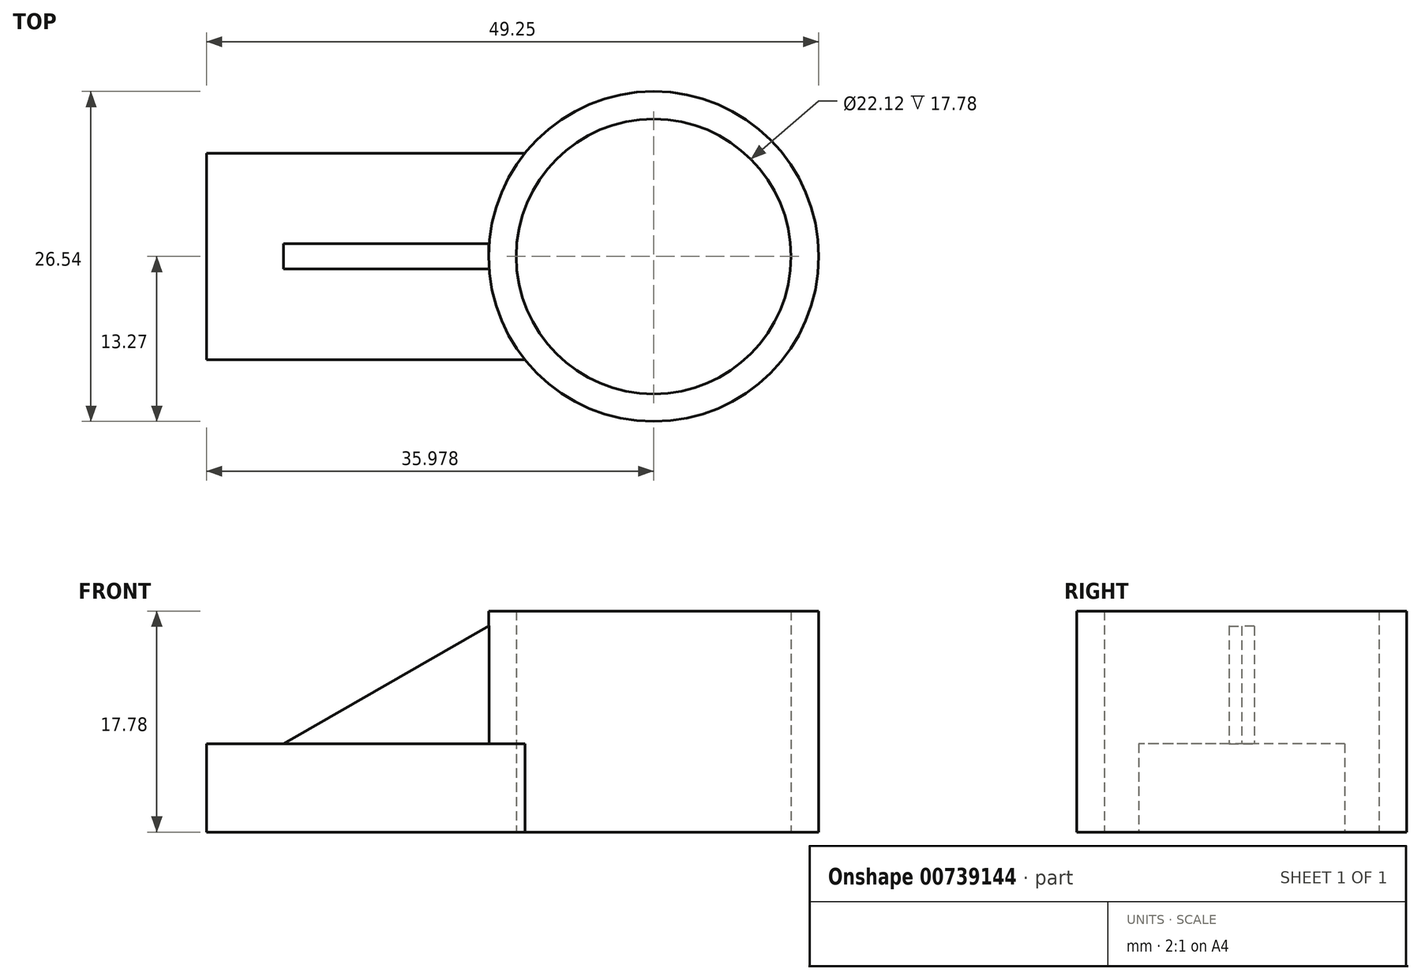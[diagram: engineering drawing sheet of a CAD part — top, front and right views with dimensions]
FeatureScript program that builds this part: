
annotation { "Feature Type Name" : "Feature", "Feature Type Description" : "" }
export const myFeature = defineFeature(function(context is Context, id is Id, definition is map)
    precondition{}
    {
        {
            var Q0;
            Q0=qCreatedBy(makeId("Top.planeOp"),FACE);
            var sketch = newSketch(context, id + "F0", { "sketchPlane" : qUnion([Q0])});
            skLineSegment(sketch, "E0.bottom", {"start": v(16.99, 8.3) * mm, "end": v(-18.99, 8.3) * mm});
            skLineSegment(sketch, "E0.top", {"start": v(16.99, -8.3) * mm, "end": v(-18.99, -8.3) * mm});
            skLineSegment(sketch, "E0.left", {"start": v(16.99, 8.3) * mm, "end": v(16.99, -8.3) * mm});
            skLineSegment(sketch, "E0.right", {"start": v(-18.99, 8.3) * mm, "end": v(-18.99, -8.3) * mm});
            skPoint(sketch, "E0.middle", {"position": v(0, 0) * mm});
            skCircle(sketch, "E1", {"center": v(16.99, 0) * mm, "radius": 13.27 * mm});
            skCircle(sketch, "E2", {"center": v(16.99, 0) * mm, "radius": 11.06 * mm});
            skSolve(sketch);
        }
        {
            var Q0;
            {var subQ0=sQuery(id+"F0.wireOp",EDGE,"E0.right");Q0=makeQuery(id+"F0.imprint","IMPRINT",FACE,{"disambiguationData":[TD([[makeQuery(id+"F0.imprint","IMPRINT",EDGE,{"derivedFrom":subQ0}),1.0]])]});}
            extrude(context, id + "F1", {"entities" : qUnion([Q0]), "depth" : 7.11 * mm, "offsetDistance" : 25.4 * mm});
        }
        {
            var Q0;
            {var subQ0=sQuery(id+"F0.wireOp",EDGE,"E1");var subQ1=sQuery(id+"F0.wireOp",EDGE,"E0.bottom");var subQ2=makeQuery(id+"F0.imprint","INTERSECT",VERTEX,{"derivedFrom":[subQ1,subQ0]});Q0=makeQuery(id+"F0.imprint","IMPRINT",FACE,{"disambiguationData":[TD([[makeQuery(id+"F0.imprint","IMPRINT",EDGE,{"disambiguationData":[TD([[subQ2,1.0]])],"derivedFrom":subQ1}),-1.0]])]});}
            var Q1;
            {var subQ0=sQuery(id+"F0.wireOp",EDGE,"E1");var subQ1=sQuery(id+"F0.wireOp",EDGE,"E0.bottom");var subQ2=makeQuery(id+"F0.imprint","INTERSECT",VERTEX,{"derivedFrom":[subQ1,subQ0]});Q1=makeQuery(id+"F0.imprint","IMPRINT",FACE,{"disambiguationData":[TD([[makeQuery(id+"F0.imprint","IMPRINT",EDGE,{"disambiguationData":[TD([[subQ2,1.0]])],"derivedFrom":subQ1}),1.0]])]});}
            extrude(context, id + "F2", {"entities" : qUnion([Q0, Q1]), "operationType" : NewBodyOperationType.ADD, "depth" : 17.78 * mm, "offsetDistance" : 25.4 * mm});
        }
        {
            var Q0;
            Q0=qCreatedBy(makeId("Front.planeOp"),FACE);
            var sketch = newSketch(context, id + "F3", { "sketchPlane" : qUnion([Q0])});
            skLineSegment(sketch, "E3", {"start": v(5.86, 7.11) * mm, "end": v(5.86, 17.78) * mm});
            skLineSegment(sketch, "E4", {"start": v(5.86, 17.78) * mm, "end": v(-12.79, 7.11) * mm});
            skLineSegment(sketch, "E5", {"start": v(-12.79, 7.11) * mm, "end": v(5.86, 7.11) * mm});
            skSolve(sketch);
        }
        {
            var Q0;
            Q0 = qSketchRegion(id + "F3", true);
            extrude(context, id + "F4", {"entities" : qUnion([Q0]), "operationType" : NewBodyOperationType.ADD, "depth" : 1.02 * mm, "offsetDistance" : 25.4 * mm});
        }
        {
            var Q0;
            Q0=makeQuery(id+"F4.opExtrude","CAP_FACE",FACE,{"disambiguationData":[OSD([sQuery(id+"F3.wireOp",EDGE,"E3"),sQuery(id+"F3.wireOp",EDGE,"E4"),sQuery(id+"F3.wireOp",EDGE,"E5")])],"isStart":true});
            extrude(context, id + "F5", {"entities" : qUnion([Q0]), "operationType" : NewBodyOperationType.ADD, "depth" : 1.02 * mm, "offsetDistance" : 25.4 * mm});
        }
    });
